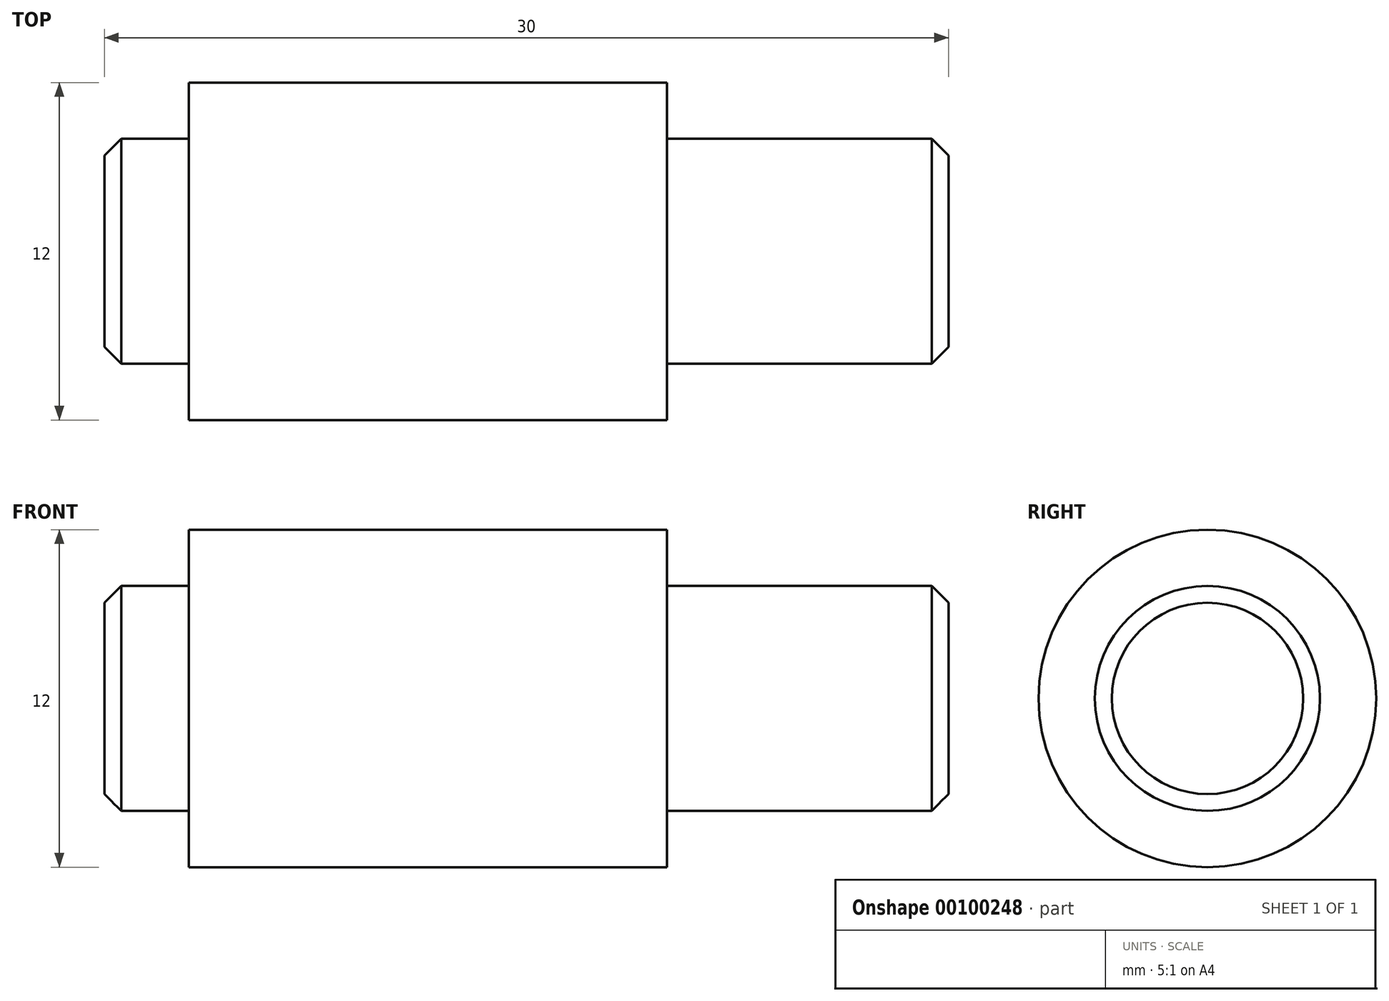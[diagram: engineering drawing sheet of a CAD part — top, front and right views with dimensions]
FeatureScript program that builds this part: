
annotation { "Feature Type Name" : "Feature", "Feature Type Description" : "" }
export const myFeature = defineFeature(function(context is Context, id is Id, definition is map)
    precondition{}
    {
        {
            var Q0;
            Q0=qCreatedBy(makeId("Front.planeOp"),FACE);
            var sketch = newSketch(context, id + "F0", { "sketchPlane" : qUnion([Q0])});
            skLineSegment(sketch, "E0", {"start": v(0, 0) * mm, "end": v(0, 3.4) * mm});
            skLineSegment(sketch, "E1", {"start": v(0.6, 4) * mm, "end": v(3, 4) * mm});
            skLineSegment(sketch, "E2", {"start": v(3, 4) * mm, "end": v(3, 6) * mm});
            skLineSegment(sketch, "E3", {"start": v(3, 6) * mm, "end": v(20, 6) * mm});
            skLineSegment(sketch, "E4", {"start": v(20, 6) * mm, "end": v(20, 4) * mm});
            skLineSegment(sketch, "E5", {"start": v(20, 4) * mm, "end": v(29.4, 4) * mm});
            skLineSegment(sketch, "E6", {"start": v(30, 3.4) * mm, "end": v(30, 0) * mm});
            skLineSegment(sketch, "E7", {"start": v(30, 0) * mm, "end": v(0, 0) * mm});
            skLineSegment(sketch, "E8", {"start": v(0.6, 4) * mm, "end": v(0, 3.4) * mm});
            skLineSegment(sketch, "E9", {"start": v(29.4, 4) * mm, "end": v(30, 3.4) * mm});
            skSolve(sketch);
        }
        {
            var Q0;
            Q0=makeQuery(id+"F0.imprint","IMPRINT",FACE,{"disambiguationData":[TD([[makeQuery(id+"F0.imprint","IMPRINT",EDGE,{"derivedFrom":sQuery(id+"F0.wireOp",EDGE,"E0")}),-1.0]])]});
            var Q1;
            Q1=sQuery(id+"F0.wireOp",EDGE,"E7");
            revolve(context, id + "F1", {"entities" : qUnion([Q0]), "axis" : qUnion([Q1]), "revolveType" : RevolveType.FULL});
        }
    });
